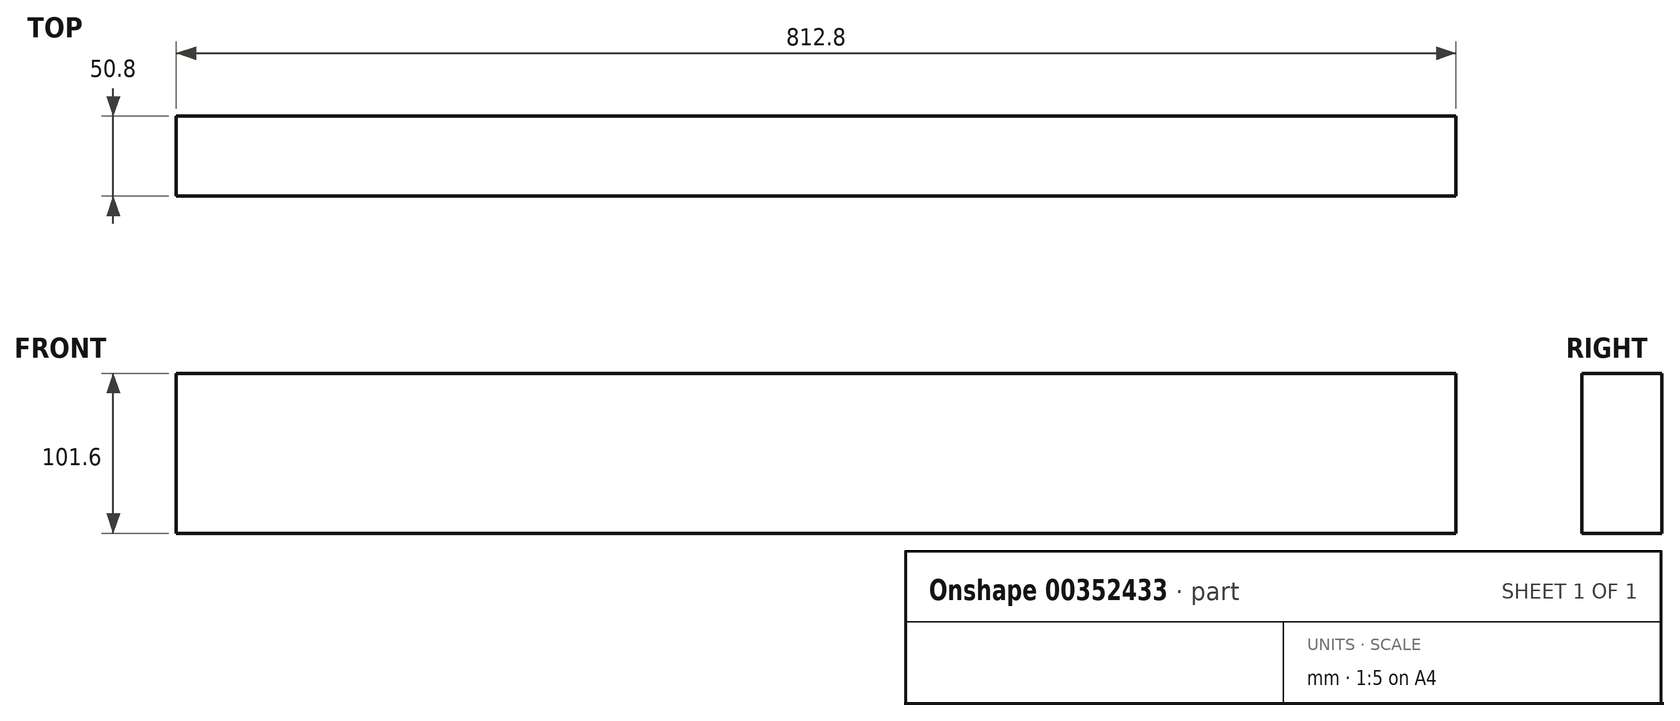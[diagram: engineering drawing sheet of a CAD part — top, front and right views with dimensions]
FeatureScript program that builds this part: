
annotation { "Feature Type Name" : "Feature", "Feature Type Description" : "" }
export const myFeature = defineFeature(function(context is Context, id is Id, definition is map)
    precondition{}
    {
        {
            var Q0;
            Q0=qCreatedBy(makeId("Right.planeOp"),FACE);
            var sketch = newSketch(context, id + "F0", { "sketchPlane" : qUnion([Q0])});
            skLineSegment(sketch, "E0.bottom", {"start": v(0, 0) * mm, "end": v(50.8, 0) * mm});
            skLineSegment(sketch, "E0.top", {"start": v(0, 101.6) * mm, "end": v(50.8, 101.6) * mm});
            skLineSegment(sketch, "E0.left", {"start": v(0, 0) * mm, "end": v(0, 101.6) * mm});
            skLineSegment(sketch, "E0.right", {"start": v(50.8, 0) * mm, "end": v(50.8, 101.6) * mm});
            skSolve(sketch);
        }
        {
            var Q0;
            Q0=makeQuery(id+"F0.imprint","IMPRINT",FACE,{"disambiguationData":[TD([[makeQuery(id+"F0.imprint","IMPRINT",EDGE,{"derivedFrom":sQuery(id+"F0.wireOp",EDGE,"E0.bottom")}),1.0]])]});
            extrude(context, id + "F1", {"entities" : qUnion([Q0]), "depth" : 812.8 * mm});
        }
    });
